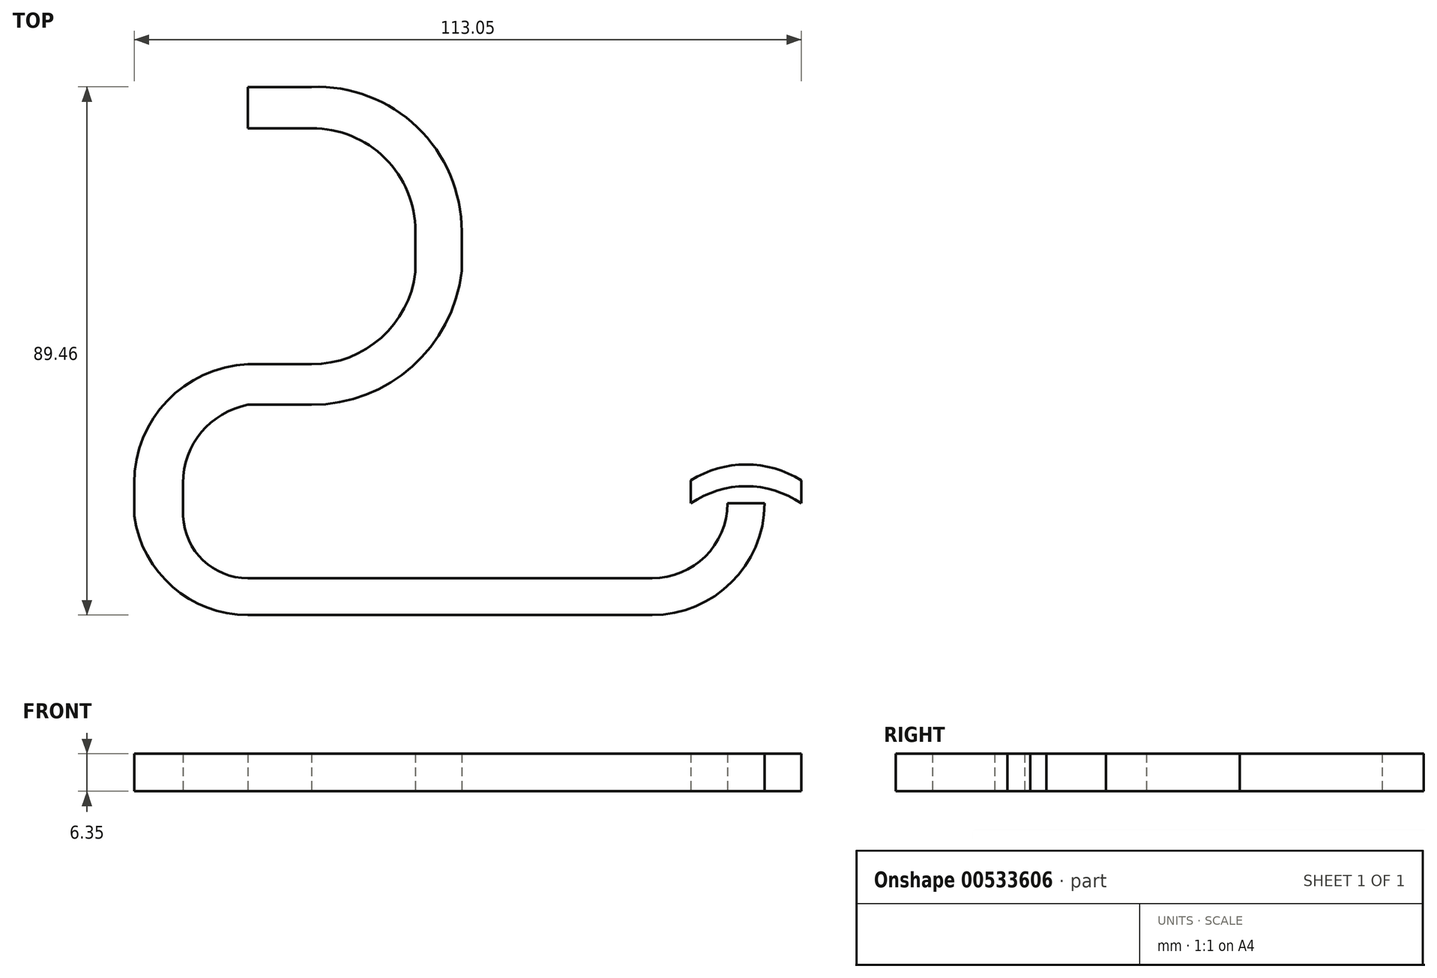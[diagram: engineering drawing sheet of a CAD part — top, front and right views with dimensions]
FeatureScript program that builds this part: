
annotation { "Feature Type Name" : "Feature", "Feature Type Description" : "" }
export const myFeature = defineFeature(function(context is Context, id is Id, definition is map)
    precondition{}
    {
        {
            var Q0;
            Q0=qCreatedBy(makeId("Top.planeOp"),FACE);
            var sketch = newSketch(context, id + "F0", { "sketchPlane" : qUnion([Q0])});
            skLineSegment(sketch, "E0.bottom", {"start": v(0, 0) * mm, "end": v(68.48, 0) * mm});
            skLineSegment(sketch, "E0.top", {"start": v(0, 6.23) * mm, "end": v(68.48, 6.23) * mm});
            skLineSegment(sketch, "E0.left", {"start": v(0, 0) * mm, "end": v(0, 6.23) * mm});
            skLineSegment(sketch, "E0.right", {"start": v(68.48, 0) * mm, "end": v(68.48, 6.23) * mm});
            skArc(sketch, "E1", {"start": v(-11.02, 16.77) * mm, "mid": v(-7.62, 9.29) * mm, "end": v(0, 6.23) * mm});
            skArc(sketch, "E2", {"start": v(-19.3, 16.77) * mm, "mid": v(-12.78, 4.78) * mm, "end": v(0, 0) * mm});
            skLineSegment(sketch, "E3.bottom", {"start": v(-11.02, 16.77) * mm, "end": v(-19.3, 16.77) * mm});
            skLineSegment(sketch, "E3.top", {"start": v(-11.02, 22.36) * mm, "end": v(-19.3, 22.36) * mm});
            skLineSegment(sketch, "E3.left", {"start": v(-11.02, 16.77) * mm, "end": v(-11.02, 22.36) * mm});
            skLineSegment(sketch, "E3.right", {"start": v(-19.3, 16.77) * mm, "end": v(-19.3, 22.36) * mm});
            skArc(sketch, "E4", {"start": v(0, 35.61) * mm, "mid": v(-7.9, 30.98) * mm, "end": v(-11.02, 22.36) * mm});
            skArc(sketch, "E5", {"start": v(0, 42.48) * mm, "mid": v(-13.7, 36.3) * mm, "end": v(-19.3, 22.36) * mm});
            skLineSegment(sketch, "E6", {"start": v(0, 42.48) * mm, "end": v(0, 35.61) * mm});
            skLineSegment(sketch, "E7.bottom", {"start": v(0, 42.48) * mm, "end": v(10.78, 42.48) * mm});
            skLineSegment(sketch, "E7.top", {"start": v(0, 35.61) * mm, "end": v(10.78, 35.61) * mm});
            skLineSegment(sketch, "E7.right", {"start": v(10.78, 42.48) * mm, "end": v(10.78, 35.61) * mm});
            skArc(sketch, "E8", {"start": v(10.78, 42.48) * mm, "mid": v(22.56, 46.96) * mm, "end": v(28.38, 58.14) * mm});
            skArc(sketch, "E9", {"start": v(10.78, 35.61) * mm, "mid": v(27.82, 42.11) * mm, "end": v(36.21, 58.3) * mm});
            skLineSegment(sketch, "E10.bottom", {"start": v(28.38, 58.14) * mm, "end": v(36.21, 58.14) * mm});
            skLineSegment(sketch, "E10.top", {"start": v(28.38, 64.99) * mm, "end": v(36.21, 64.99) * mm});
            skLineSegment(sketch, "E10.left", {"start": v(28.38, 58.14) * mm, "end": v(28.38, 64.99) * mm});
            skLineSegment(sketch, "E10.right", {"start": v(36.21, 58.14) * mm, "end": v(36.21, 64.99) * mm});
            skArc(sketch, "E11", {"start": v(28.38, 64.99) * mm, "mid": v(23.22, 77.38) * mm, "end": v(10.78, 82.43) * mm});
            skArc(sketch, "E12", {"start": v(36.21, 64.99) * mm, "mid": v(28.7, 82.63) * mm, "end": v(10.78, 89.44) * mm});
            skLineSegment(sketch, "E13.bottom", {"start": v(10.78, 89.44) * mm, "end": v(0, 89.44) * mm});
            skLineSegment(sketch, "E13.top", {"start": v(10.78, 82.43) * mm, "end": v(0, 82.43) * mm});
            skLineSegment(sketch, "E13.left", {"start": v(10.78, 89.44) * mm, "end": v(10.78, 82.43) * mm});
            skLineSegment(sketch, "E13.right", {"start": v(0, 89.44) * mm, "end": v(0, 82.43) * mm});
            skArc(sketch, "E14", {"start": v(68.48, 6.23) * mm, "mid": v(77.48, 9.94) * mm, "end": v(81.25, 18.91) * mm});
            skArc(sketch, "E15", {"start": v(68.48, 0) * mm, "mid": v(81.91, 5.53) * mm, "end": v(87.55, 18.91) * mm});
            skLineSegment(sketch, "E16", {"start": v(81.25, 18.91) * mm, "end": v(87.55, 18.91) * mm});
            skArc(sketch, "E17", {"start": v(93.76, 18.91) * mm, "mid": v(84.4, 21.82) * mm, "end": v(75.05, 18.91) * mm});
            skArc(sketch, "E18", {"start": v(93.76, 22.8) * mm, "mid": v(84.4, 25.5) * mm, "end": v(75.05, 22.8) * mm});
            skLineSegment(sketch, "E19", {"start": v(75.05, 22.8) * mm, "end": v(75.05, 18.91) * mm});
            skLineSegment(sketch, "E20", {"start": v(93.76, 22.8) * mm, "end": v(93.76, 18.91) * mm});
            skSolve(sketch);
        }
        {
            var Q0;
            Q0=makeQuery(id+"F0.imprint","IMPRINT",FACE,{"disambiguationData":[TD([[makeQuery(id+"F0.imprint","IMPRINT",EDGE,{"derivedFrom":sQuery(id+"F0.wireOp",EDGE,"E3.top")}),-1.0]])]});
            var Q1;
            Q1=makeQuery(id+"F0.imprint","IMPRINT",FACE,{"disambiguationData":[TD([[makeQuery(id+"F0.imprint","IMPRINT",EDGE,{"derivedFrom":sQuery(id+"F0.wireOp",EDGE,"E3.bottom")}),-1.0]])]});
            var Q2;
            Q2=makeQuery(id+"F0.imprint","IMPRINT",FACE,{"disambiguationData":[TD([[makeQuery(id+"F0.imprint","IMPRINT",EDGE,{"derivedFrom":sQuery(id+"F0.wireOp",EDGE,"E0.left")}),1.0]])]});
            var Q3;
            Q3=makeQuery(id+"F0.imprint","IMPRINT",FACE,{"disambiguationData":[TD([[makeQuery(id+"F0.imprint","IMPRINT",EDGE,{"derivedFrom":sQuery(id+"F0.wireOp",EDGE,"E0.bottom")}),1.0]])]});
            var Q4;
            Q4=makeQuery(id+"F0.imprint","IMPRINT",FACE,{"disambiguationData":[TD([[makeQuery(id+"F0.imprint","IMPRINT",EDGE,{"derivedFrom":sQuery(id+"F0.wireOp",EDGE,"E7.bottom")}),-1.0]])]});
            var Q5;
            {var subQ0=sQuery(id+"F0.wireOp",EDGE,"E7.right");Q5=makeQuery(id+"F0.imprint","IMPRINT",FACE,{"disambiguationData":[TD([[makeQuery(id+"F0.imprint","IMPRINT",EDGE,{"derivedFrom":subQ0}),1.0]])]});}
            var Q6;
            {var subQ1=sQuery(id+"F0.wireOp",EDGE,"E10.top");Q6=makeQuery(id+"F0.imprint","IMPRINT",FACE,{"disambiguationData":[TD([[makeQuery(id+"F0.imprint","IMPRINT",EDGE,{"derivedFrom":subQ1}),-1.0]])]});}
            var Q7;
            Q7=makeQuery(id+"F0.imprint","IMPRINT",FACE,{"disambiguationData":[TD([[makeQuery(id+"F0.imprint","IMPRINT",EDGE,{"derivedFrom":sQuery(id+"F0.wireOp",EDGE,"E10.top")}),1.0]])]});
            var Q8;
            Q8=makeQuery(id+"F0.imprint","IMPRINT",FACE,{"disambiguationData":[TD([[makeQuery(id+"F0.imprint","IMPRINT",EDGE,{"derivedFrom":sQuery(id+"F0.wireOp",EDGE,"E13.bottom")}),1.0]])]});
            var Q9;
            Q9=makeQuery(id+"F0.imprint","IMPRINT",FACE,{"disambiguationData":[TD([[makeQuery(id+"F0.imprint","IMPRINT",EDGE,{"derivedFrom":sQuery(id+"F0.wireOp",EDGE,"E0.right")}),-1.0]])]});
            var Q10;
            Q10=makeQuery(id+"F0.imprint","IMPRINT",FACE,{"disambiguationData":[TD([[makeQuery(id+"F0.imprint","IMPRINT",EDGE,{"derivedFrom":sQuery(id+"F0.wireOp",EDGE,"E17")}),-1.0]])]});
            extrude(context, id + "F1", {"entities" : qUnion([Q0, Q1, Q2, Q3, Q4, Q5, Q6, Q7, Q8, Q9, Q10]), "depth" : 6.35 * mm, "offsetDistance" : 25.4 * mm});
        }
    });
